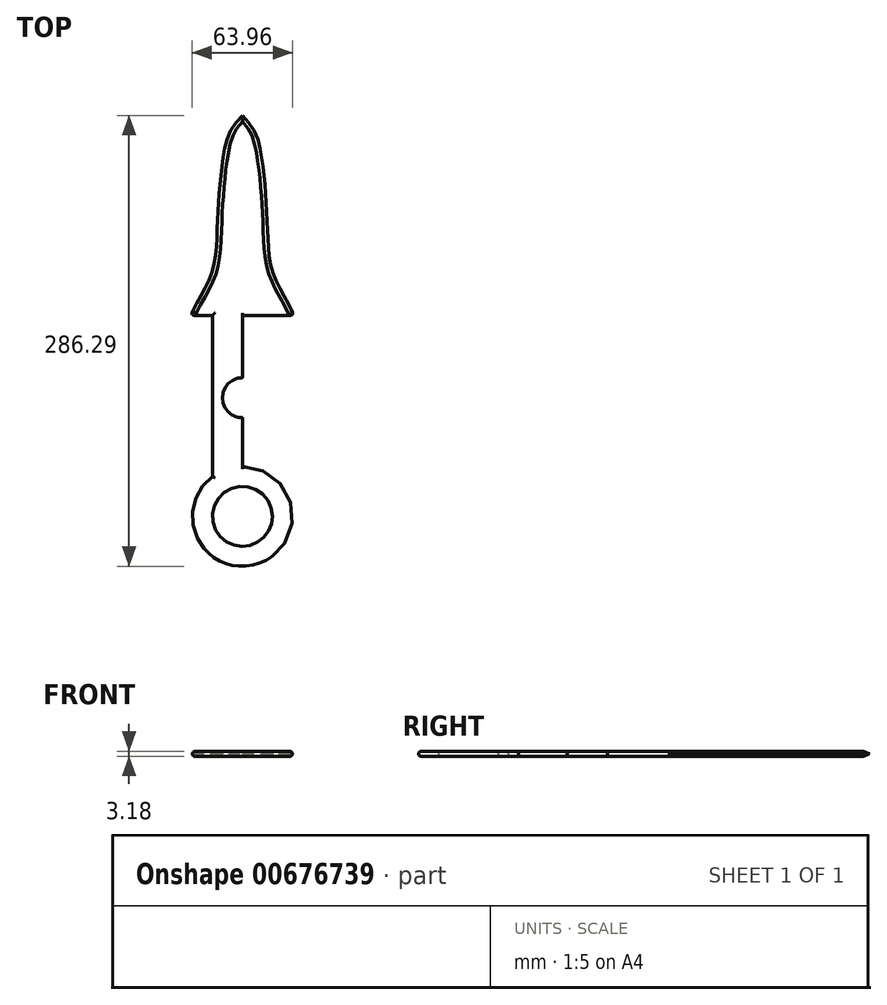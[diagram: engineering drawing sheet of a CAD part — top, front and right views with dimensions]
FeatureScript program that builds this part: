
annotation { "Feature Type Name" : "Feature", "Feature Type Description" : "" }
export const myFeature = defineFeature(function(context is Context, id is Id, definition is map)
    precondition{}
    {
        {
            var Q0;
            Q0=qCreatedBy(makeId("Top.planeOp"),FACE);
            var sketch = newSketch(context, id + "F0", { "sketchPlane" : qUnion([Q0])});
            skLineSegment(sketch, "E0", {"start": v(0, 127) * mm, "end": v(0, 0) * mm});
            skLineSegment(sketch, "E1", {"start": v(0, 0) * mm, "end": v(38.1, 0) * mm});
            skLineSegment(sketch, "E2", {"start": v(0, 0) * mm, "end": v(-38.1, 0) * mm});
            skFitSpline(sketch, "E3", {"points": [v(0, 127) * mm, v(7.48, 117.69) * mm, v(12.86, 96.2) * mm, v(15.93, 57.06) * mm, v(19.76, 26.36) * mm, v(30.9, 4.49) * mm, v(32.43, 0) * mm], "startDerivative": vector(64.25, -64.22) * mm, "endDerivative": vector(10.43, -46.14) * mm});
            skFitSpline(sketch, "E4.MirrorCS", {"points": [v(0, 127) * mm, v(-7.48, 117.69) * mm, v(-12.86, 96.2) * mm, v(-15.93, 57.06) * mm, v(-19.76, 26.36) * mm, v(-30.9, 4.49) * mm, v(-32.43, 0) * mm], "startDerivative": vector(-64.25, -64.22) * mm, "endDerivative": vector(-10.43, -46.14) * mm});
            skPoint(sketch, "E5.oppositeSnap0", {"position": v(19.05, 0) * mm});
            skLineSegment(sketch, "E5.bottom", {"start": v(0, 0) * mm, "end": v(19.05, 0) * mm});
            skLineSegment(sketch, "E5.left", {"start": v(0, 0) * mm, "end": v(0, -95.85) * mm});
            skLineSegment(sketch, "E5.right", {"start": v(19.05, 0) * mm, "end": v(19.05, -102.96) * mm});
            skLineSegment(sketch, "E6.MirrorCS", {"start": v(-19.05, 0) * mm, "end": v(-19.05, -102.96) * mm});
            skCircle(sketch, "E7", {"center": v(0, -127.6) * mm, "radius": 31.75 * mm});
            skCircle(sketch, "E8", {"center": v(0, -127.6) * mm, "radius": 19.05 * mm});
            skPoint(sketch, "E9.MirrorCS.end.orphan", {"position": v(-19.05, -102.96) * mm});
            skPoint(sketch, "E9.MirrorCS.start.orphan", {"position": v(0, -102.96) * mm});
            skCircle(sketch, "E10", {"center": v(0, -52.27) * mm, "radius": 12.7 * mm});
            skSolve(sketch);
        }
        {
            var Q0;
            {var subQ0=sQuery(id+"F0.wireOp",EDGE,"E0");Q0=makeQuery(id+"F0.imprint","IMPRINT",FACE,{"disambiguationData":[TD([[makeQuery(id+"F0.imprint","IMPRINT",EDGE,{"derivedFrom":subQ0}),-1.0]])]});}
            var Q1;
            Q1=makeQuery(id+"F0.imprint","IMPRINT",FACE,{"disambiguationData":[TD([[makeQuery(id+"F0.imprint","IMPRINT",EDGE,{"derivedFrom":sQuery(id+"F0.wireOp",EDGE,"E0")}),1.0]])]});
            var Q2;
            {var subQ0=sQuery(id+"F0.wireOp",EDGE,"E5.left");Q2=makeQuery(id+"F0.imprint","IMPRINT",FACE,{"disambiguationData":[TD([[makeQuery(id+"F0.imprint","IMPRINT",EDGE,{"derivedFrom":subQ0}),-1.0]])]});}
            var Q3;
            {var subQ0=sQuery(id+"F0.wireOp",EDGE,"E5.bottom");Q3=makeQuery(id+"F0.imprint","IMPRINT",FACE,{"disambiguationData":[TD([[makeQuery(id+"F0.imprint","IMPRINT",EDGE,{"derivedFrom":subQ0}),-1.0]])]});}
            var Q4;
            Q4=makeQuery(id+"F0.imprint","IMPRINT",FACE,{"disambiguationData":[TD([[makeQuery(id+"F0.imprint","IMPRINT",EDGE,{"derivedFrom":sQuery(id+"F0.wireOp",EDGE,"E8")}),-1.0]])]});
            extrude(context, id + "F1", {"entities" : qUnion([Q0, Q1, Q2, Q3, Q4]), "depth" : 3.17 * mm, "offsetDistance" : 25.4 * mm});
        }
        {
            var Q0;
            Q0=makeQuery(id+"F1.opExtrude","CAP_EDGE",EDGE,{"disambiguationData":[OSD([sQuery(id+"F0.wireOp",EDGE,"E4.MirrorCS")])],"isStart":false});
            var Q1;
            Q1=makeQuery(id+"F1.opExtrude","CAP_EDGE",EDGE,{"disambiguationData":[OSD([sQuery(id+"F0.wireOp",EDGE,"E4.MirrorCS")])],"isStart":true});
            var Q2;
            Q2=makeQuery(id+"F1.opExtrude","CAP_EDGE",EDGE,{"disambiguationData":[OSD([sQuery(id+"F0.wireOp",EDGE,"E3")])],"isStart":true});
            var Q3;
            Q3=makeQuery(id+"F1.opExtrude","CAP_EDGE",EDGE,{"disambiguationData":[OSD([sQuery(id+"F0.wireOp",EDGE,"E3")])],"isStart":false});
            chamfer(context, id + "F2", {"entities" : qUnion([Q0, Q1, Q2, Q3]), "chamferType" : ChamferType.OFFSET_ANGLE, "width" : 2.8 * mm, "oppositeDirection" : false, "angle" : 30 * degree, "tangentPropagation" : true});
        }
        {
            var Q0;
            Q0=makeQuery(id+"F1.opExtrude","CAP_EDGE",EDGE,{"disambiguationData":[OSD([sQuery(id+"F0.wireOp",EDGE,"E6.MirrorCS")])],"isStart":false});
            var Q1;
            Q1=makeQuery(id+"F1.opExtrude","CAP_EDGE",EDGE,{"disambiguationData":[OSD([sQuery(id+"F0.wireOp",EDGE,"E5.right")])],"isStart":false});
            var Q2;
            Q2=makeQuery(id+"F1.opExtrude","CAP_EDGE",EDGE,{"disambiguationData":[OSD([sQuery(id+"F0.wireOp",EDGE,"E5.right")])],"isStart":true});
            var Q3;
            Q3=makeQuery(id+"F1.opExtrude","CAP_EDGE",EDGE,{"disambiguationData":[OSD([sQuery(id+"F0.wireOp",EDGE,"E6.MirrorCS")])],"isStart":true});
            var Q4;
            Q4=makeQuery(id+"F1.opExtrude","CAP_EDGE",EDGE,{"disambiguationData":[OSD([sQuery(id+"F0.wireOp",EDGE,"E1")])],"isStart":true});
            var Q5;
            Q5=makeQuery(id+"F1.opExtrude","CAP_EDGE",EDGE,{"disambiguationData":[OSD([sQuery(id+"F0.wireOp",EDGE,"E2")])],"isStart":true});
            var Q6;
            Q6=makeQuery(id+"F2.opChamfer","BLEND_EDGE",EDGE,{"blendedFrom":[makeQuery(id+"F1.opExtrude","CAP_EDGE",EDGE,{"disambiguationData":[OSD([sQuery(id+"F0.wireOp",EDGE,"E3")])],"isStart":true}),makeQuery(id+"F1.opExtrude","SWEPT_FACE",FACE,{"disambiguationData":[OSD([sQuery(id+"F0.wireOp",EDGE,"E1")])]})],"blendedInto":[makeQuery(id+"F1.opExtrude","SWEPT_FACE",FACE,{"disambiguationData":[OSD([sQuery(id+"F0.wireOp",EDGE,"E1")])]})]});
            var Q7;
            Q7=makeQuery(id+"F1.opExtrude","CAP_EDGE",EDGE,{"disambiguationData":[OSD([sQuery(id+"F0.wireOp",EDGE,"E2")])],"isStart":false});
            var Q8;
            Q8=makeQuery(id+"F2.opChamfer","BLEND_EDGE",EDGE,{"blendedFrom":[makeQuery(id+"F1.opExtrude","CAP_EDGE",EDGE,{"disambiguationData":[OSD([sQuery(id+"F0.wireOp",EDGE,"E4.MirrorCS")])],"isStart":false}),makeQuery(id+"F1.opExtrude","SWEPT_FACE",FACE,{"disambiguationData":[OSD([sQuery(id+"F0.wireOp",EDGE,"E2")])]})],"blendedInto":[makeQuery(id+"F1.opExtrude","SWEPT_FACE",FACE,{"disambiguationData":[OSD([sQuery(id+"F0.wireOp",EDGE,"E2")])]})]});
            var Q9;
            Q9=makeQuery(id+"F2.opChamfer","BLEND_EDGE",EDGE,{"blendedFrom":[makeQuery(id+"F1.opExtrude","CAP_EDGE",EDGE,{"disambiguationData":[OSD([sQuery(id+"F0.wireOp",EDGE,"E3")])],"isStart":false}),makeQuery(id+"F1.opExtrude","SWEPT_FACE",FACE,{"disambiguationData":[OSD([sQuery(id+"F0.wireOp",EDGE,"E1")])]})],"blendedInto":[makeQuery(id+"F1.opExtrude","SWEPT_FACE",FACE,{"disambiguationData":[OSD([sQuery(id+"F0.wireOp",EDGE,"E1")])]})]});
            var Q10;
            Q10=makeQuery(id+"F1.opExtrude","CAP_EDGE",EDGE,{"disambiguationData":[OSD([sQuery(id+"F0.wireOp",EDGE,"E1")])],"isStart":false});
            var Q11;
            Q11=makeQuery(id+"F2.opChamfer","BLEND_EDGE",EDGE,{"blendedFrom":[makeQuery(id+"F1.opExtrude","CAP_EDGE",EDGE,{"disambiguationData":[OSD([sQuery(id+"F0.wireOp",EDGE,"E4.MirrorCS")])],"isStart":true}),makeQuery(id+"F1.opExtrude","SWEPT_FACE",FACE,{"disambiguationData":[OSD([sQuery(id+"F0.wireOp",EDGE,"E2")])]})],"blendedInto":[makeQuery(id+"F1.opExtrude","SWEPT_FACE",FACE,{"disambiguationData":[OSD([sQuery(id+"F0.wireOp",EDGE,"E2")])]})]});
            var Q12;
            Q12=makeQuery(id+"F1.opExtrude","CAP_EDGE",EDGE,{"disambiguationData":[OSD([sQuery(id+"F0.wireOp",EDGE,"E8")])],"isStart":true});
            var Q13;
            Q13=makeQuery(id+"F1.opExtrude","CAP_EDGE",EDGE,{"disambiguationData":[OSD([sQuery(id+"F0.wireOp",EDGE,"E7")])],"isStart":true});
            var Q14;
            Q14=makeQuery(id+"F1.opExtrude","CAP_EDGE",EDGE,{"disambiguationData":[OSD([sQuery(id+"F0.wireOp",EDGE,"E7")])],"isStart":false});
            var Q15;
            Q15=makeQuery(id+"F1.opExtrude","CAP_EDGE",EDGE,{"disambiguationData":[OSD([sQuery(id+"F0.wireOp",EDGE,"E8")])],"isStart":false});
            var Q16;
            Q16=makeQuery(id+"F1.opExtrude","CAP_EDGE",EDGE,{"disambiguationData":[OSD([sQuery(id+"F0.wireOp",EDGE,"E10")])],"isStart":true});
            var Q17;
            Q17=makeQuery(id+"F1.opExtrude","CAP_EDGE",EDGE,{"disambiguationData":[OSD([sQuery(id+"F0.wireOp",EDGE,"E10")])],"isStart":false});
            fillet(context, id + "F3", {"entities" : qUnion([Q0, Q1, Q2, Q3, Q4, Q5, Q6, Q7, Q8, Q9, Q10, Q11, Q12, Q13, Q14, Q15, Q16, Q17]), "radius" : 1.59 * mm, "tangentPropagation" : true, "allowEdgeOverflow" : false});
        }
    });
